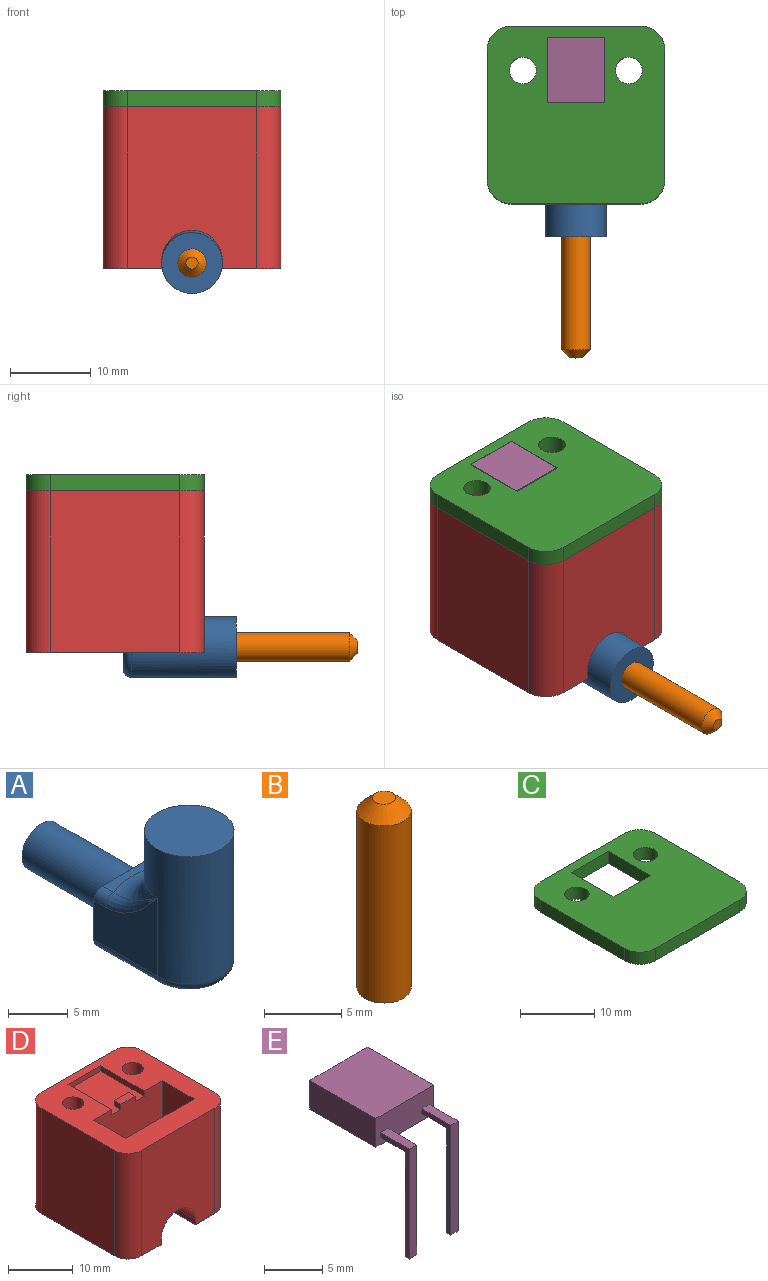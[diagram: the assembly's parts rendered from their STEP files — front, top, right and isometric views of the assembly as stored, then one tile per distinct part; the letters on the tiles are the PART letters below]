
ASSEMBLY  parts=5 mates=5
PART A: 17 faces, bbox 19.2x21.6x14 mm
  f0: cylinder r=3.75mm len=13mm, axis (0,0,1), area 212.1mm2, adj f2,f3,f4,f7,f11
  f1: plane 10.25x5.5mm, normal (0,0,-1), area 53.1mm2, adj f6,f10,f11,f12
  f2: plane 7.5x7.5mm, normal (0,0,1), area 44.2mm2, adj f0
  f3: plane 8x7.5mm, normal (-1,0,0), area 38.2mm2, adj f0,f6,f10,f15,f16
  f4: plane 8x7.5mm, normal (1,0,0), area 38.2mm2, adj f0,f6,f12,f13,f14
  f5: plane 5.5x1.34mm, normal (0,0,1), area 5.2mm2, adj f6,f7,f13,f15
  f6: plane 7.5x6mm, normal (0,1,0), area 28.2mm2, adj f1,f3,f4,f5,f8,f10,f12,f13
  f7: torus R=6.75mm, axis (0,0,-1), area 36.3mm2, adj f0,f5,f14,f16
  f8: cylinder r=2.25mm len=10mm, axis (0,-1,0), area 141.4mm2, adj f6,f9
  f9: plane 4.5x4.5mm, normal (0,1,0), area 15.9mm2, adj f8
  f10: cylinder r=1mm len=7.5mm, axis (0,-1,0), area 11.8mm2, adj f1,f3,f6,f11
  f11: torus R=2.75mm, axis (0,0,1), area 16.7mm2, adj f0,f1,f10,f12
  f12: cylinder r=1mm len=7.5mm, axis (0,1,0), area 11.8mm2, adj f1,f4,f6,f11
  f13: cylinder r=1mm len=1.34mm, axis (0,1,0), area 2.1mm2, adj f4,f5,f6,f14
  f14: bspline ~7.31x4mm, area 6.5mm2, adj f4,f7,f13
  f15: cylinder r=1mm len=1.34mm, axis (0,-1,0), area 2.1mm2, adj f3,f5,f6,f16
  f16: bspline ~7.31x4mm, area 6.5mm2, adj f3,f7,f15
PART B: 4 faces, bbox 3.5x3.5x15 mm
  f0: cylinder r=1.75mm len=14mm, axis (0,0,-1), area 153.9mm2, adj f2,f3
  f1: plane 1.5x1.5mm, normal (0,0,1), area 1.8mm2, adj f3
  f2: plane 3.5x3.5mm, normal (0,0,-1), area 9.6mm2, adj f0
  f3: cone r=0.75mm half-angle=45deg, axis (0,0,-1), area 11.1mm2, adj f0,f1
PART C: 16 faces, bbox 22x22x2 mm
  f0: plane 16x2mm, normal (0,1,0), area 32mm2, adj f10,f11,f12,f15
  f1: plane 16x2mm, normal (-1,0,0), area 32mm2, adj f10,f11,f12,f13
  f2: plane 16x2mm, normal (0,-1,0), area 32mm2, adj f10,f11,f13,f14
  f3: plane 8.1x2mm, normal (-1,0,0), area 16.2mm2, adj f4,f8,f10,f11
  f4: plane 7.1x2mm, normal (0,1,0), area 14.2mm2, adj f3,f5,f10,f11
  f5: plane 8.1x2mm, normal (1,0,0), area 16.2mm2, adj f4,f8,f10,f11
  f6: cylinder r=1.65mm len=3.3mm, axis (0,0,-1), area 20.7mm2, adj f10,f11
  f7: cylinder r=1.65mm len=3.3mm, axis (0,0,-1), area 20.7mm2, adj f10,f11
  f8: plane 7.1x2mm, normal (0,-1,0), area 14.2mm2, adj f3,f5,f10,f11
  f9: plane 16x2mm, normal (1,0,0), area 32mm2, adj f10,f11,f14,f15
  f10: plane 22x22mm, normal (0,0,1), area 401.7mm2, adj f0,f1,f2,f3,f4,f5,f6,f7
  f11: plane 22x22mm, normal (0,0,-1), area 401.7mm2, adj f0,f1,f2,f3,f4,f5,f6,f7
  f12: cylinder r=3mm len=3mm, axis (0,0,1), area 9.4mm2, adj f0,f1,f10,f11
  f13: cylinder r=3mm len=3mm, axis (0,0,-1), area 9.4mm2, adj f1,f2,f10,f11
  f14: cylinder r=3mm len=3mm, axis (0,0,1), area 9.4mm2, adj f2,f9,f10,f11
  f15: cylinder r=3mm len=3mm, axis (0,0,-1), area 9.4mm2, adj f0,f9,f10,f11
PART D: 43 faces, bbox 22x22x20 mm
  f0: cylinder r=1.65mm len=10mm, axis (0,0,1), area 103.7mm2, adj f2,f38
  f1: cylinder r=1.65mm len=10mm, axis (0,0,1), area 103.7mm2, adj f2,f31
  f2: plane 22x22mm, normal (0,0,1), area 286mm2, adj f0,f1,f6,f7,f8,f9,f13,f15
  f3: plane 3.1x1.5mm, normal (0,0,1), area 4.6mm2, adj f16,f21,f22,f23
  f4: plane 15x7mm, normal (0,0,1), area 60mm2, adj f5,f10,f11,f13,f15,f16,f17
  f5: plane 10x8mm, normal (-1,0,0), area 52mm2, adj f4,f9,f11,f12,f13,f14
  f6: plane 20x16mm, normal (1,0,0), area 320mm2, adj f2,f12,f39,f40
  f7: plane 20x16mm, normal (0,1,0), area 320mm2, adj f2,f12,f40,f41
  f8: plane 20x16mm, normal (-1,0,0), area 320mm2, adj f2,f12,f41,f42
  f9: plane 20x16mm, normal (0,-1,0), area 290.4mm2, adj f2,f5,f10,f12,f14,f39,f42
  f10: plane 10x8mm, normal (1,0,0), area 52mm2, adj f4,f9,f11,f12,f13,f14
  f11: plane 8x7.5mm, normal (0,-1,0), area 60mm2, adj f4,f5,f10,f12
  f12: plane 22x22mm, normal (0,0,-1), area 344.7mm2, adj f5,f6,f7,f8,f9,f10,f11,f25
  f13: plane 19x15mm, normal (0,1,0), area 210.4mm2, adj f2,f4,f5,f10,f14,f15,f17
  f14: cylinder r=3.75mm len=7.5mm, axis (0,-1,0), area 47.1mm2, adj f5,f9,f10,f13
  f15: plane 12x7mm, normal (1,0,0), area 84mm2, adj f2,f4,f13,f16
  f16: plane 15x12mm, normal (0,-1,0), area 176mm2, adj f2,f3,f4,f15,f17,f18,f20,f21
  f17: plane 12x7mm, normal (-1,0,0), area 84mm2, adj f2,f4,f13,f16
  f18: plane 9.6x1mm, normal (-1,0,0), area 9.6mm2, adj f2,f16,f19,f24
  f19: plane 7.1x1mm, normal (0,-1,0), area 7.1mm2, adj f2,f18,f20,f24
  f20: plane 9.6x1mm, normal (1,0,0), area 9.6mm2, adj f2,f16,f19,f24
  f21: plane 1.5x1mm, normal (-1,0,0), area 1.5mm2, adj f3,f16,f22,f24
  f22: plane 3.1x1mm, normal (0,1,0), area 3.1mm2, adj f3,f21,f23,f24
  f23: plane 1.5x1mm, normal (1,0,0), area 1.5mm2, adj f3,f16,f22,f24
  f24: plane 9.6x7.1mm, normal (0,0,1), area 63.5mm2, adj f16,f18,f19,f20,f21,f22,f23
  f25: plane 10x2.86mm, normal (0.5,-0.87,0), area 33mm2, adj f12,f26,f30,f31
  f26: plane 10x2.86mm, normal (-0.5,-0.87,0), area 33mm2, adj f12,f25,f27,f31
  f27: plane 10x3.3mm, normal (-1,0,0), area 33mm2, adj f12,f26,f28,f31
  f28: plane 10x2.86mm, normal (-0.5,0.87,0), area 33mm2, adj f12,f27,f29,f31
  f29: plane 10x2.86mm, normal (0.5,0.87,0), area 33mm2, adj f12,f28,f30,f31
  f30: plane 10x3.3mm, normal (1,0,0), area 33mm2, adj f12,f25,f29,f31
  f31: plane 6.6x5.72mm, normal (0,0,-1), area 19.7mm2, adj f1,f25,f26,f27,f28,f29,f30
  f32: plane 10x2.86mm, normal (0.5,-0.87,0), area 33mm2, adj f12,f33,f37,f38
  f33: plane 10x2.86mm, normal (-0.5,-0.87,0), area 33mm2, adj f12,f32,f34,f38
  f34: plane 10x3.3mm, normal (-1,0,0), area 33mm2, adj f12,f33,f35,f38
  f35: plane 10x2.86mm, normal (-0.5,0.87,0), area 33mm2, adj f12,f34,f36,f38
  f36: plane 10x2.86mm, normal (0.5,0.87,0), area 33mm2, adj f12,f35,f37,f38
  f37: plane 10x3.3mm, normal (1,0,0), area 33mm2, adj f12,f32,f36,f38
  f38: plane 6.6x5.72mm, normal (0,0,-1), area 19.7mm2, adj f0,f32,f33,f34,f35,f36,f37
  f39: cylinder r=3mm len=20mm, axis (0,0,1), area 94.2mm2, adj f2,f6,f9,f12
  f40: cylinder r=3mm len=20mm, axis (0,0,-1), area 94.2mm2, adj f2,f6,f7,f12
  f41: cylinder r=3mm len=20mm, axis (0,0,1), area 94.2mm2, adj f2,f7,f8,f12
  f42: cylinder r=3mm len=20mm, axis (0,0,-1), area 94.2mm2, adj f2,f8,f9,f12
PART E: 20 faces, bbox 7x11.5x13.3 mm
  f0: plane 3x0.9mm, normal (0,0,-1), area 2.7mm2, adj f4,f13,f14,f18
  f1: plane 3x0.9mm, normal (0,0,-1), area 2.7mm2, adj f4,f9,f10,f16
  f2: plane 7x3mm, normal (0,1,0), area 21mm2, adj f3,f5,f6,f7
  f3: plane 8x3mm, normal (-1,0,0), area 24mm2, adj f2,f4,f6,f7
  f4: plane 7x3mm, normal (0,-1,0), area 20.1mm2, adj f0,f1,f3,f5,f6,f7,f8,f9
  f5: plane 8x3mm, normal (1,0,0), area 24mm2, adj f2,f4,f6,f7
  f6: plane 8x7mm, normal (0,0,1), area 56mm2, adj f2,f3,f4,f5
  f7: plane 8x7mm, normal (0,0,-1), area 56mm2, adj f2,f3,f4,f5
  f8: plane 3.5x0.9mm, normal (0,0,1), area 3.1mm2, adj f4,f9,f10,f11
  f9: plane 11.5x3.5mm, normal (-1,0,0), area 7.2mm2, adj f1,f4,f8,f11,f16,f17
  f10: plane 11.5x3.5mm, normal (1,0,0), area 7.2mm2, adj f1,f4,f8,f11,f16,f17
  f11: plane 11.5x0.9mm, normal (0,-1,0), area 10.3mm2, adj f8,f9,f10,f17
  f12: plane 3.5x0.9mm, normal (0,0,1), area 3.1mm2, adj f4,f13,f14,f15
  f13: plane 11.5x3.5mm, normal (-1,0,0), area 7.2mm2, adj f0,f4,f12,f15,f18,f19
  f14: plane 11.5x3.5mm, normal (1,0,0), area 7.2mm2, adj f0,f4,f12,f15,f18,f19
  f15: plane 11.5x0.9mm, normal (0,-1,0), area 10.3mm2, adj f12,f13,f14,f19
  f16: plane 11x0.9mm, normal (0,1,0), area 9.9mm2, adj f1,f9,f10,f17
  f17: plane 0.9x0.5mm, normal (0,0,-1), area 0.4mm2, adj f9,f10,f11,f16
  f18: plane 11x0.9mm, normal (0,1,0), area 9.9mm2, adj f0,f13,f14,f19
  f19: plane 0.9x0.5mm, normal (0,0,-1), area 0.4mm2, adj f13,f14,f15,f18
PLACE A rot(axis=(1,0,0),90deg) t=(0,-15,0.68)mm
PLACE B rot(axis=(1,0,0),90deg) t=(0,-15,0.68)mm
PLACE C t=(0,0,-20)mm
PLACE D at identity fixed
PLACE E t=(0,5.6,19)mm
MATE planar E.f7 <-> D.f24  axis (0,0,-1) through (0,5.6,19)mm
MATE slider D.f0 <-> C.f6  axis (0,0,1) through (6.55,5.5,20)mm
MATE planar A.f0 <-> D.f11  axis (0,1,0) through (0,-1,0.68)mm
MATE fastened B.f0 <-> A.f0  axis (0,1,0) through (0,-15,0.68)mm
MATE planar E.f2 <-> D.f19  axis (0,1,0) through (0,9.6,20.5)mm
